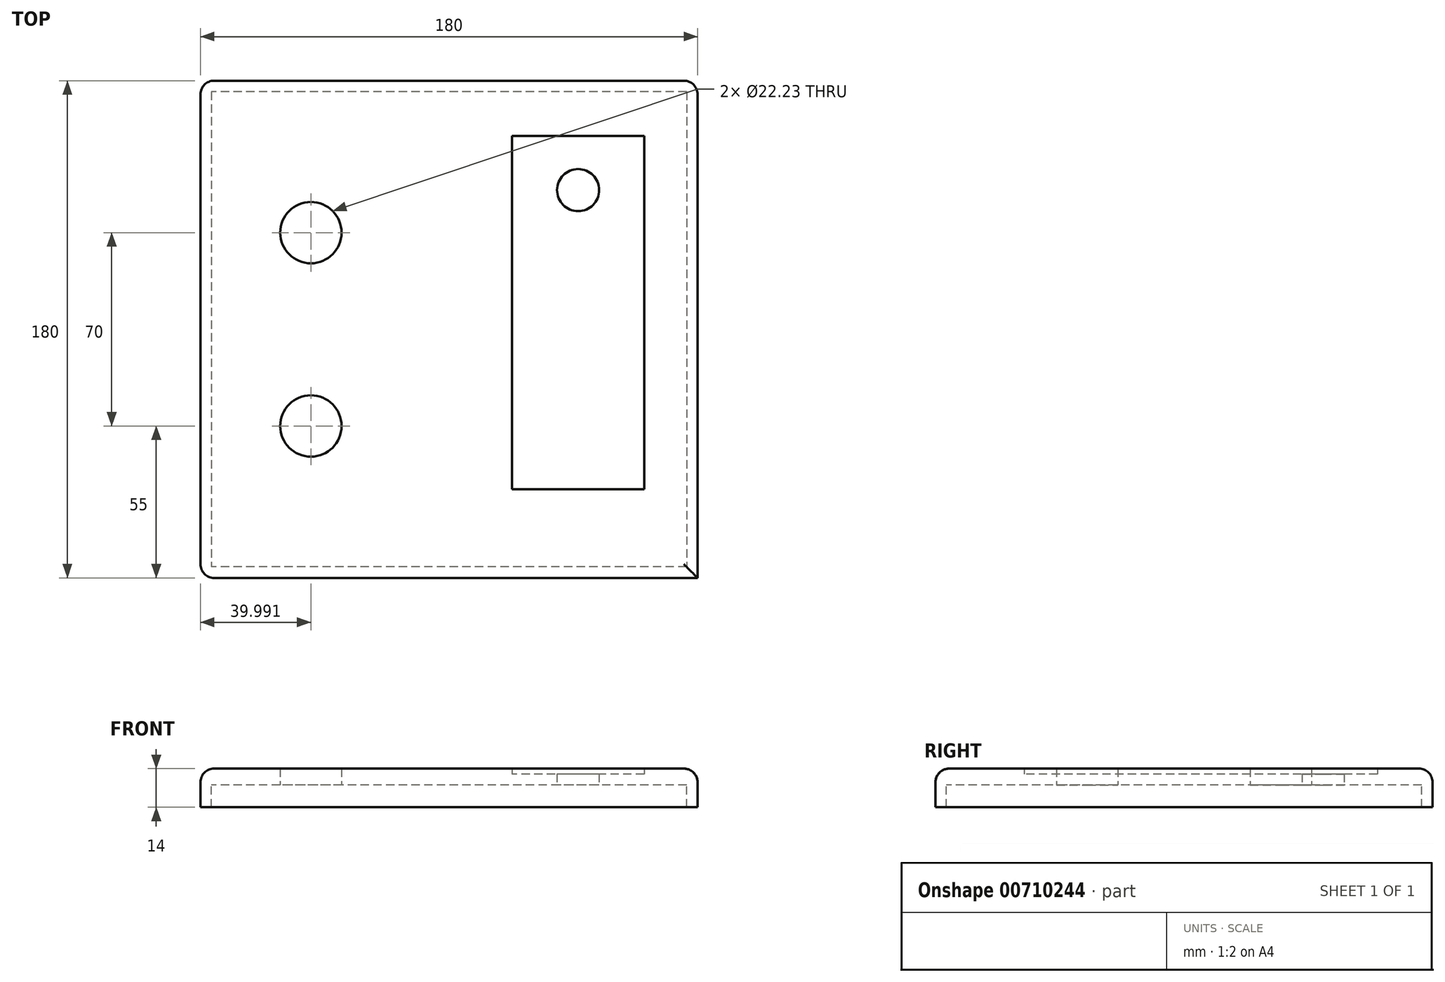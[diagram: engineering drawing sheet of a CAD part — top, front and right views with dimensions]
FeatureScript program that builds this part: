
annotation { "Feature Type Name" : "Feature", "Feature Type Description" : "" }
export const myFeature = defineFeature(function(context is Context, id is Id, definition is map)
    precondition{}
    {
        {
            var Q0;
            Q0=qCreatedBy(makeId("Top.planeOp"),FACE);
            var sketch = newSketch(context, id + "F0", { "sketchPlane" : qUnion([Q0])});
            skLineSegment(sketch, "E0.bottom", {"start": v(90, -90) * mm, "end": v(-90, -90) * mm});
            skLineSegment(sketch, "E0.top", {"start": v(90, 90) * mm, "end": v(-90, 90) * mm});
            skLineSegment(sketch, "E0.left", {"start": v(90, -90) * mm, "end": v(90, 90) * mm});
            skLineSegment(sketch, "E0.right", {"start": v(-90, -90) * mm, "end": v(-90, 90) * mm});
            skPoint(sketch, "E0.middle", {"position": v(0, 0) * mm});
            skLineSegment(sketch, "E1", {"start": v(-50, 90) * mm, "end": v(-50, -90) * mm, "construction": true});
            skLineSegment(sketch, "E2.bottom", {"start": v(70.63, 70.05) * mm, "end": v(22.84, 70.05) * mm});
            skLineSegment(sketch, "E2.top", {"start": v(70.63, -57.9) * mm, "end": v(22.84, -57.9) * mm});
            skLineSegment(sketch, "E2.left", {"start": v(70.63, 70.05) * mm, "end": v(70.63, -57.9) * mm});
            skLineSegment(sketch, "E2.right", {"start": v(22.84, 70.05) * mm, "end": v(22.84, -57.9) * mm});
            skCircle(sketch, "E3", {"center": v(46.73, 50.4) * mm, "radius": 7.62 * mm});
            skCircle(sketch, "E4", {"center": v(-50, 35) * mm, "radius": 11.11 * mm});
            skCircle(sketch, "E5", {"center": v(-50, -35) * mm, "radius": 11.11 * mm});
            skSolve(sketch);
        }
        {
            var Q0;
            Q0=makeQuery(id+"F0.imprint","IMPRINT",FACE,{"disambiguationData":[TD([[makeQuery(id+"F0.imprint","IMPRINT",EDGE,{"derivedFrom":sQuery(id+"F0.wireOp",EDGE,"E0.bottom")}),-1.0]])]});
            extrude(context, id + "F1", {"entities" : qUnion([Q0]), "depth" : 6 * mm, "offsetDistance" : 25 * mm});
        }
        {
            var Q0;
            Q0=makeQuery(id+"F0.imprint","IMPRINT",FACE,{"disambiguationData":[TD([[makeQuery(id+"F0.imprint","IMPRINT",EDGE,{"derivedFrom":sQuery(id+"F0.wireOp",EDGE,"E2.bottom")}),1.0]])]});
            extrude(context, id + "F2", {"entities" : qUnion([Q0]), "operationType" : NewBodyOperationType.ADD, "depth" : 4 * mm, "offsetDistance" : 25 * mm});
        }
        {
            var Q0;
            Q0=qCreatedBy(makeId("Top.planeOp"),FACE);
            var sketch = newSketch(context, id + "F3", { "sketchPlane" : qUnion([Q0])});
            skLineSegment(sketch, "E6.0.0", {"start": v(90, -90) * mm, "end": v(90, 90) * mm});
            skLineSegment(sketch, "E6.0.1", {"start": v(90, 90) * mm, "end": v(-90, 90) * mm});
            skLineSegment(sketch, "E6.0.2", {"start": v(-90, 90) * mm, "end": v(-90, -90) * mm});
            skLineSegment(sketch, "E6.0.3", {"start": v(-90, -90) * mm, "end": v(90, -90) * mm});
            skLineSegment(sketch, "E7.bottom", {"start": v(86, 86) * mm, "end": v(-86, 86) * mm});
            skLineSegment(sketch, "E7.top", {"start": v(86, -86) * mm, "end": v(-86, -86) * mm});
            skLineSegment(sketch, "E7.left", {"start": v(86, 86) * mm, "end": v(86, -86) * mm});
            skLineSegment(sketch, "E7.right", {"start": v(-86, 86) * mm, "end": v(-86, -86) * mm});
            skPoint(sketch, "E7.middle", {"position": v(0, 0) * mm});
            skSolve(sketch);
        }
        {
            var Q0;
            Q0=makeQuery(id+"F3.imprint","IMPRINT",FACE,{"disambiguationData":[TD([[makeQuery(id+"F3.imprint","IMPRINT",EDGE,{"derivedFrom":sQuery(id+"F3.wireOp",EDGE,"E6.0.0")}),1.0]])]});
            extrude(context, id + "F4", {"entities" : qUnion([Q0]), "operationType" : NewBodyOperationType.ADD, "oppositeDirection" : true, "depth" : 8 * mm, "offsetDistance" : 25 * mm});
        }
        {
            var Q0;
            Q0=makeQuery(id+"F1.opExtrude","CAP_EDGE",EDGE,{"disambiguationData":[OSD([sQuery(id+"F0.wireOp",EDGE,"E0.right")])],"isStart":false});
            var Q1;
            Q1=makeQuery(id+"F1.opExtrude","CAP_EDGE",EDGE,{"disambiguationData":[OSD([sQuery(id+"F0.wireOp",EDGE,"E0.bottom")])],"isStart":false});
            var Q2;
            Q2=makeQuery(id+"F1.opExtrude","CAP_EDGE",EDGE,{"disambiguationData":[OSD([sQuery(id+"F0.wireOp",EDGE,"E0.left")])],"isStart":false});
            var Q3;
            Q3=makeQuery(id+"F4.boolean.opBoolean","MERGE",EDGE,{"derivedFrom":[makeQuery(id+"F1.opExtrude","SWEPT_EDGE",EDGE,{"disambiguationData":[OSD([sQuery(id+"F0.wireOp",EDGE,"E0.top"),sQuery(id+"F0.wireOp",EDGE,"E0.left")])]}),makeQuery(id+"F4.opExtrude","SWEPT_EDGE",EDGE,{"disambiguationData":[OSD([sQuery(id+"F3.wireOp",EDGE,"E6.0.0"),sQuery(id+"F3.wireOp",EDGE,"E6.0.1")])]})]});
            var Q4;
            Q4=makeQuery(id+"F1.opExtrude","CAP_EDGE",EDGE,{"disambiguationData":[OSD([sQuery(id+"F0.wireOp",EDGE,"E0.top")])],"isStart":false});
            var Q5;
            Q5=makeQuery(id+"F4.boolean.opBoolean","MERGE",EDGE,{"derivedFrom":[makeQuery(id+"F1.opExtrude","SWEPT_EDGE",EDGE,{"disambiguationData":[OSD([sQuery(id+"F0.wireOp",EDGE,"E0.top"),sQuery(id+"F0.wireOp",EDGE,"E0.right")])]}),makeQuery(id+"F4.opExtrude","SWEPT_EDGE",EDGE,{"disambiguationData":[OSD([sQuery(id+"F3.wireOp",EDGE,"E6.0.1"),sQuery(id+"F3.wireOp",EDGE,"E6.0.2")])]})]});
            var Q6;
            Q6=makeQuery(id+"F4.boolean.opBoolean","MERGE",EDGE,{"derivedFrom":[makeQuery(id+"F1.opExtrude","SWEPT_EDGE",EDGE,{"disambiguationData":[OSD([sQuery(id+"F0.wireOp",EDGE,"E0.bottom"),sQuery(id+"F0.wireOp",EDGE,"E0.right")])]}),makeQuery(id+"F4.opExtrude","SWEPT_EDGE",EDGE,{"disambiguationData":[OSD([sQuery(id+"F3.wireOp",EDGE,"E6.0.2"),sQuery(id+"F3.wireOp",EDGE,"E6.0.3")])]})]});
            fillet(context, id + "F5", {"entities" : qUnion([Q0, Q1, Q2, Q3, Q4, Q5, Q6]), "radius" : 5 * mm, "tangentPropagation" : true, "allowEdgeOverflow" : false});
        }
    });
